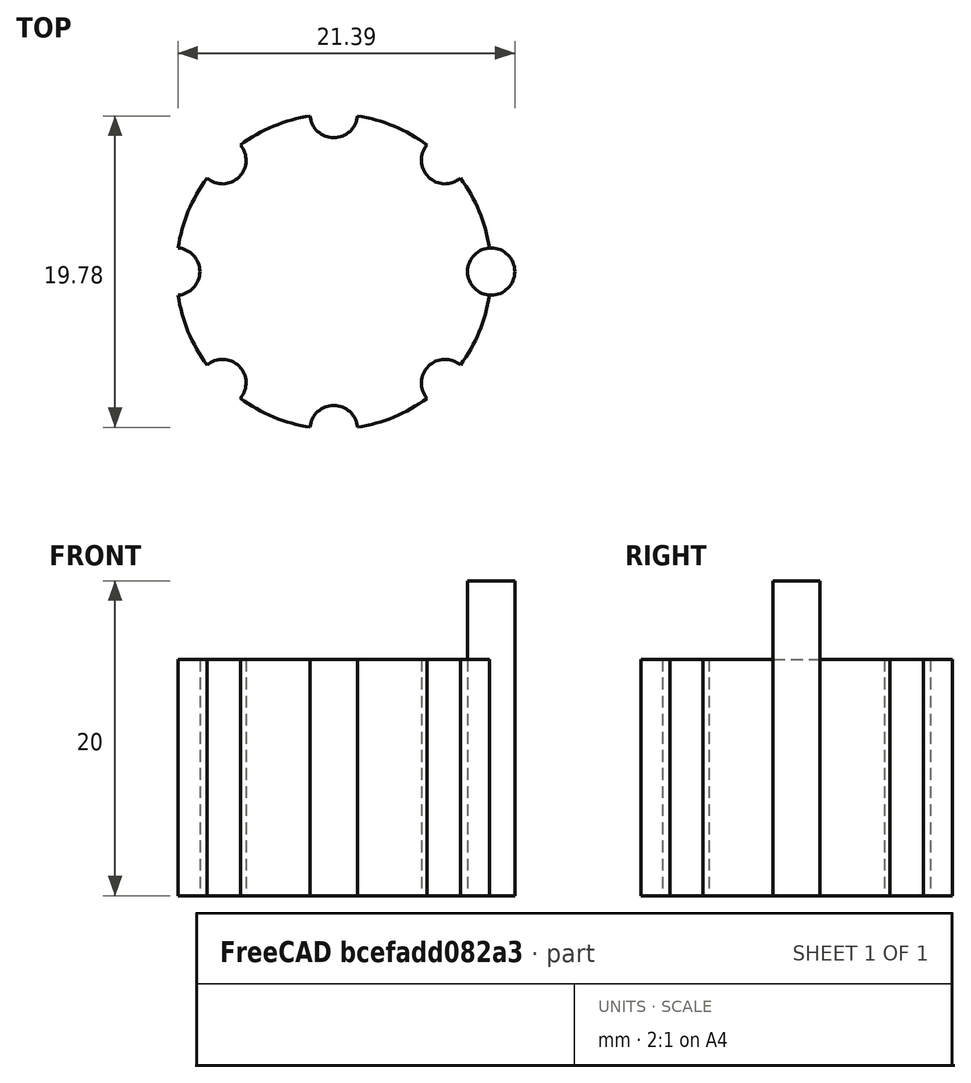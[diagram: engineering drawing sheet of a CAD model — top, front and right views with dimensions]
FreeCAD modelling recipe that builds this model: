
FCSTD DOCUMENT  (FreeCAD 0.21R33694 (Git))
Label: OJT1_T11R01_boto
License: All rights reserved
LicenseURL: http://en.wikipedia.org/wiki/All_rights_reserved
objects: Part::Cylinder×2, Part::FeaturePython×1, Part::Cut×1
note: 3 computed .brp shape members not serialized (recipe doc carries the construction recipe); baked Part::Feature solids carry a one-line shape summary decoded from their .brp

FEATURE [Part::Cylinder] Cylinder
  Angle = 360
  AttacherType = Attacher::AttachEngine3D
  FirstAngle = 0
  Height = 15
  Radius = 10
  SecondAngle = 0
FEATURE [Part::Cylinder] Cylinder001
  Angle = 360
  AttacherType = Attacher::AttachEngine3D
  FirstAngle = 0
  Height = 20
  Placement = pos=(10,0,0) rot=(0,0,1;0rad)
  Radius = 1.5
  SecondAngle = 0
FEATURE [Part::FeaturePython] Array  # Draft array (typed FeaturePython)
  AlwaysSyncPlacement = false
  Angle = 360
  ArrayType = 1
  Axis = (0,0,1)
  Base = -> Cylinder001
  Center = (0,0,0)
  Count = 8
  ExpandArray = false
  Fuse = false
  IntervalAxis = (0,0,0)
  IntervalX = (50,0,0)
  IntervalY = (0,50,0)
  IntervalZ = (0,0,50)
  NumberCircles = 3
  NumberPolar = 8
  NumberX = 2
  NumberY = 2
  NumberZ = 1
  PlacementList = 8 placements: [(10,0,0),(7.07107,7.07107,0),(0,10,0),(-7.07107,7.07107,0),(-10,1.22465e-15,0),(-7.07107,-7.07107,0),(-2.22045e-15,-10,0),(7.07107,-7.07107,0)]
  RadialDistance = 50
  ScaleList = (8) [(1,1,1),(1,1,1),(1,1,1),(1,1,1),(1,1,1),(1,1,1),(1,1,1),(1,1,1)]
  Symmetry = 1
  TangentialDistance = 25
FEATURE [Part::Cut] Cut
  Base = -> Cylinder
  Refine = true
  Tool = -> Array
